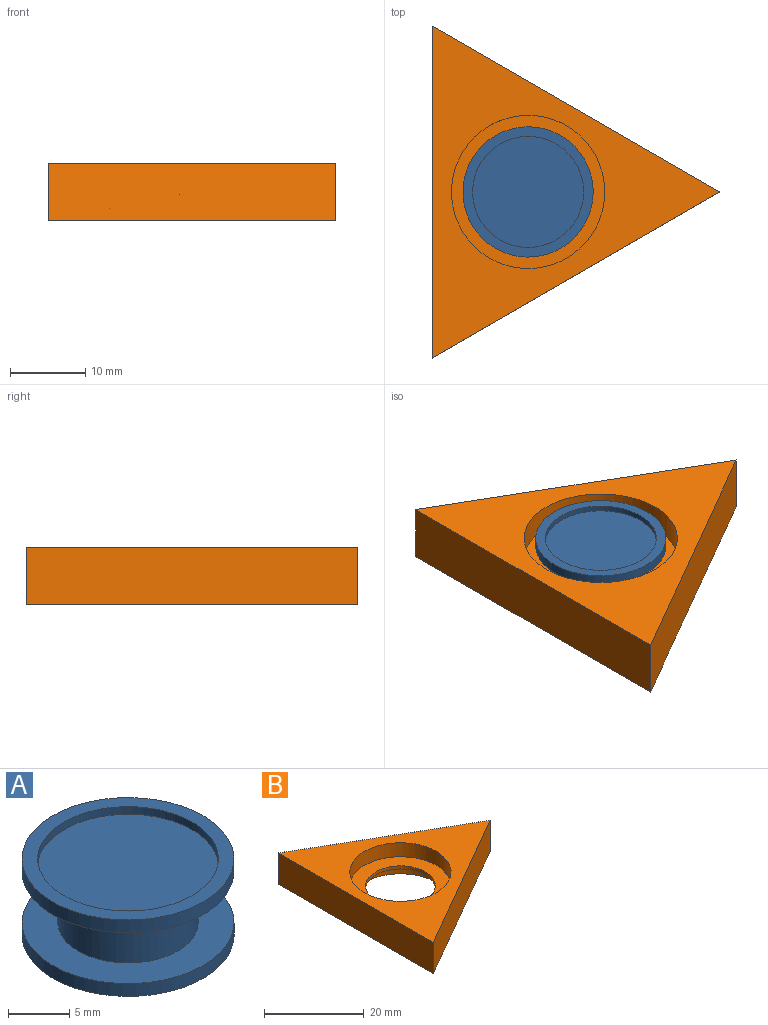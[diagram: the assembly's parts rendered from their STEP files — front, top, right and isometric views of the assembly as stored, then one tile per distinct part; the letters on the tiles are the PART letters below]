
ASSEMBLY  parts=2 mates=1
PART A: 11 faces, bbox 17.3x17.3x7.6 mm
  f0: cylinder r=5.71mm len=11.43mm, axis (0,0,-1), area 182.4mm2, adj f2,f5
  f1: cylinder r=8.64mm len=17.27mm, axis (0,0,1), area 68.9mm2, adj f2,f3
  f2: plane 17.27x17.27mm, normal (0,0,-1), area 131.7mm2, adj f0,f1
  f3: plane 17.27x17.27mm, normal (0,0,1), area 63.8mm2, adj f1,f9
  f4: cylinder r=8.64mm len=17.27mm, axis (0,0,-1), area 68.9mm2, adj f5,f6
  f5: plane 17.27x17.27mm, normal (0,0,1), area 131.7mm2, adj f0,f4
  f6: plane 17.27x17.27mm, normal (0,0,-1), area 63.8mm2, adj f4,f7
  f7: cylinder r=7.37mm len=14.73mm, axis (0,0,-1), area 35.3mm2, adj f6,f8
  f8: plane 14.73x14.73mm, normal (0,0,-1), area 170.5mm2, adj f7
  f9: cylinder r=7.37mm len=14.73mm, axis (0,0,1), area 35.3mm2, adj f3,f10
  f10: plane 14.73x14.73mm, normal (0,0,1), area 170.5mm2, adj f9
PART B: 10 faces, bbox 38.1x44x7.6 mm
  f0: cylinder r=6.99mm len=13.97mm, axis (0,0,-1), area 33.4mm2, adj f7,f9
  f1: plane 43.99x7.62mm, normal (-1,0,0), area 335.2mm2, adj f2,f3,f4,f5
  f2: plane 38.1x22mm, normal (0.5,-0.87,0), area 335.2mm2, adj f1,f3,f4,f5
  f3: plane 38.1x22mm, normal (0.5,0.87,0), area 335.2mm2, adj f1,f2,f4,f5
  f4: plane 43.99x38.1mm, normal (0,0,1), area 513.8mm2, adj f1,f2,f3,f8
  f5: plane 43.99x38.1mm, normal (0,0,-1), area 513.8mm2, adj f1,f2,f3,f6
  f6: cylinder r=10.16mm len=20.32mm, axis (0,0,-1), area 218.9mm2, adj f5,f7
  f7: plane 20.32x20.32mm, normal (0,0,-1), area 171mm2, adj f0,f6
  f8: cylinder r=10.16mm len=20.32mm, axis (0,0,1), area 218.9mm2, adj f4,f9
  f9: plane 20.32x20.32mm, normal (0,0,1), area 171mm2, adj f0,f8
PLACE A t=(-14.92,-0.8,2.6)mm
PLACE B t=(-14.92,-0.8,2.6)mm
MATE fastened A.f0 <-> B.f0  axis (0,0,-1) through (-14.92,-0.8,6.41)mm
